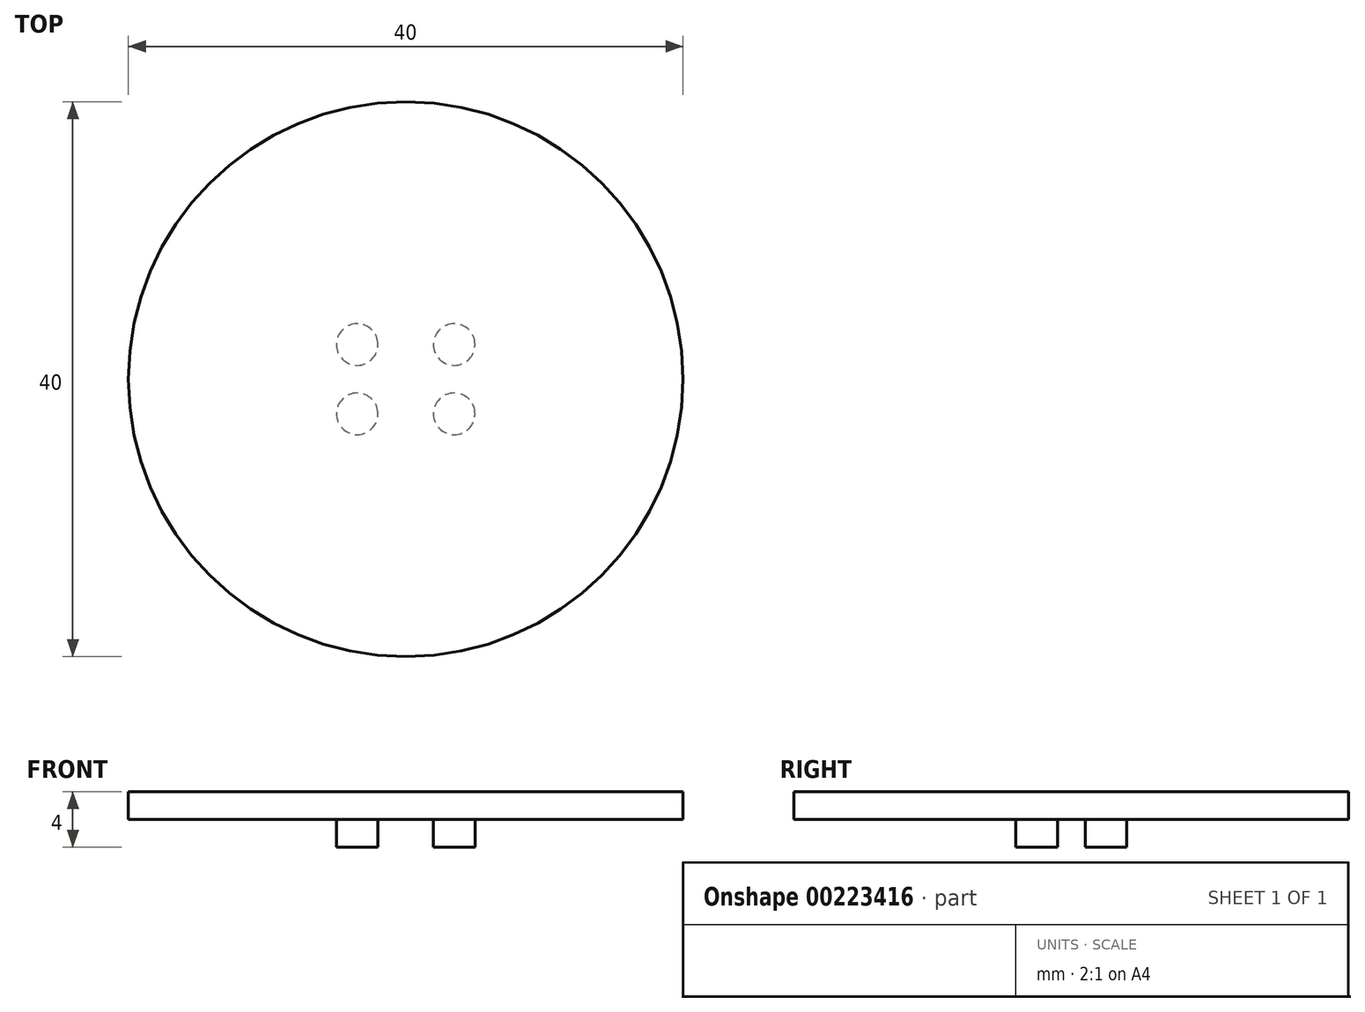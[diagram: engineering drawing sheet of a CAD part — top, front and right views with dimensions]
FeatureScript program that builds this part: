
annotation { "Feature Type Name" : "Feature", "Feature Type Description" : "" }
export const myFeature = defineFeature(function(context is Context, id is Id, definition is map)
    precondition{}
    {
        {
            var Q0;
            Q0=qCreatedBy(makeId("Top.planeOp"),FACE);
            var sketch = newSketch(context, id + "F0", { "sketchPlane" : qUnion([Q0])});
            skCircle(sketch, "E0", {"center": v(0, 0) * mm, "radius": 20 * mm});
            skLineSegment(sketch, "E1.bottom", {"start": v(3.5, -2.5) * mm, "end": v(-3.5, -2.5) * mm, "construction": true});
            skLineSegment(sketch, "E1.top", {"start": v(3.5, 2.5) * mm, "end": v(-3.5, 2.5) * mm, "construction": true});
            skLineSegment(sketch, "E1.left", {"start": v(3.5, -2.5) * mm, "end": v(3.5, 2.5) * mm, "construction": true});
            skLineSegment(sketch, "E1.right", {"start": v(-3.5, -2.5) * mm, "end": v(-3.5, 2.5) * mm, "construction": true});
            skCircle(sketch, "E2", {"center": v(-3.5, 2.5) * mm, "radius": 1.5 * mm});
            skCircle(sketch, "E3", {"center": v(3.5, 2.5) * mm, "radius": 1.5 * mm});
            skCircle(sketch, "E4", {"center": v(3.5, -2.5) * mm, "radius": 1.5 * mm});
            skCircle(sketch, "E5", {"center": v(-3.5, -2.5) * mm, "radius": 1.5 * mm});
            skSolve(sketch);
        }
        {
            var Q0;
            Q0=makeQuery(id+"F0.imprint","IMPRINT",FACE,{"disambiguationData":[TD([[makeQuery(id+"F0.imprint","IMPRINT",EDGE,{"derivedFrom":sQuery(id+"F0.wireOp",EDGE,"E3")}),1.0]])]});
            var Q1;
            Q1=makeQuery(id+"F0.imprint","IMPRINT",FACE,{"disambiguationData":[TD([[makeQuery(id+"F0.imprint","IMPRINT",EDGE,{"derivedFrom":sQuery(id+"F0.wireOp",EDGE,"E2")}),1.0]])]});
            var Q2;
            Q2=makeQuery(id+"F0.imprint","IMPRINT",FACE,{"disambiguationData":[TD([[makeQuery(id+"F0.imprint","IMPRINT",EDGE,{"derivedFrom":sQuery(id+"F0.wireOp",EDGE,"E0")}),1.0]])]});
            var Q3;
            Q3=makeQuery(id+"F0.imprint","IMPRINT",FACE,{"disambiguationData":[TD([[makeQuery(id+"F0.imprint","IMPRINT",EDGE,{"derivedFrom":sQuery(id+"F0.wireOp",EDGE,"E4")}),1.0]])]});
            var Q4;
            Q4=makeQuery(id+"F0.imprint","IMPRINT",FACE,{"disambiguationData":[TD([[makeQuery(id+"F0.imprint","IMPRINT",EDGE,{"derivedFrom":sQuery(id+"F0.wireOp",EDGE,"E5")}),1.0]])]});
            extrude(context, id + "F1", {"entities" : qUnion([Q0, Q1, Q2, Q3, Q4]), "depth" : 2 * mm});
        }
        {
            var Q0;
            Q0=makeQuery(id+"F0.imprint","IMPRINT",FACE,{"disambiguationData":[TD([[makeQuery(id+"F0.imprint","IMPRINT",EDGE,{"derivedFrom":sQuery(id+"F0.wireOp",EDGE,"E2")}),1.0]])]});
            var Q1;
            Q1=makeQuery(id+"F0.imprint","IMPRINT",FACE,{"disambiguationData":[TD([[makeQuery(id+"F0.imprint","IMPRINT",EDGE,{"derivedFrom":sQuery(id+"F0.wireOp",EDGE,"E5")}),1.0]])]});
            var Q2;
            Q2=makeQuery(id+"F0.imprint","IMPRINT",FACE,{"disambiguationData":[TD([[makeQuery(id+"F0.imprint","IMPRINT",EDGE,{"derivedFrom":sQuery(id+"F0.wireOp",EDGE,"E4")}),1.0]])]});
            var Q3;
            Q3=makeQuery(id+"F0.imprint","IMPRINT",FACE,{"disambiguationData":[TD([[makeQuery(id+"F0.imprint","IMPRINT",EDGE,{"derivedFrom":sQuery(id+"F0.wireOp",EDGE,"E3")}),1.0]])]});
            extrude(context, id + "F2", {"entities" : qUnion([Q0, Q1, Q2, Q3]), "operationType" : NewBodyOperationType.ADD, "oppositeDirection" : true, "depth" : 2 * mm});
        }
    });
